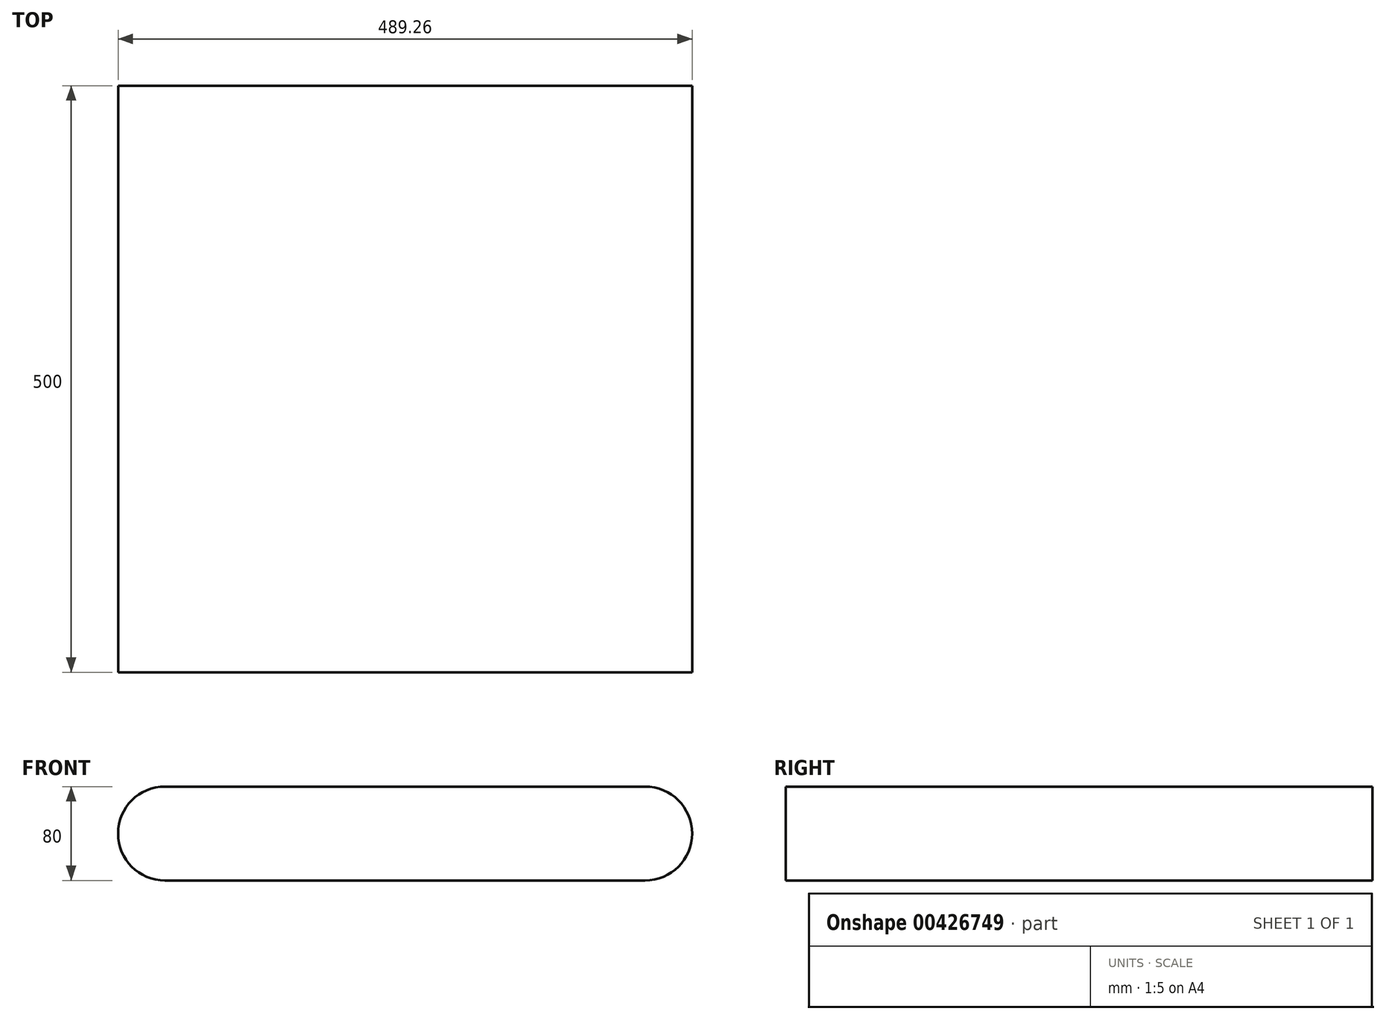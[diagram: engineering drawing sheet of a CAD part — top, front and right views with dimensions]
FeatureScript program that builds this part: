
annotation { "Feature Type Name" : "Feature", "Feature Type Description" : "" }
export const myFeature = defineFeature(function(context is Context, id is Id, definition is map)
    precondition{}
    {
        {
            var Q0;
            Q0=qCreatedBy(makeId("Front.planeOp"),FACE);
            var sketch = newSketch(context, id + "F0", { "sketchPlane" : qUnion([Q0])});
            skArc(sketch, "E0", {"start": v(0, -40) * mm, "mid": v(40, 0) * mm, "end": v(0, 40) * mm});
            skLineSegment(sketch, "E1", {"start": v(0, 40) * mm, "end": v(-409.26, 40) * mm});
            skLineSegment(sketch, "E2", {"start": v(0, -40) * mm, "end": v(-409.26, -40) * mm});
            skLineSegment(sketch, "E3", {"start": v(-449.25, -1.02) * mm, "end": v(-449.25, -1.02) * mm});
            skPoint(sketch, "E4.visualSharp", {"position": v(-450.3, 40) * mm});
            skArc(sketch, "E4.filletArc", {"start": v(-409.26, 40) * mm, "mid": v(-437.9, 27.92) * mm, "end": v(-449.25, -1.02) * mm});
            skPoint(sketch, "E5.visualSharp", {"position": v(-448.25, -40) * mm});
            skArc(sketch, "E5.filletArc", {"start": v(-449.25, -1.02) * mm, "mid": v(-437.18, -28.64) * mm, "end": v(-409.26, -40) * mm});
            skSolve(sketch);
        }
        {
            var Q0;
            Q0=makeQuery(id+"F0.imprint","IMPRINT",FACE,{"disambiguationData":[TD([[makeQuery(id+"F0.imprint","IMPRINT",EDGE,{"derivedFrom":sQuery(id+"F0.wireOp",EDGE,"E0")}),1.0]])]});
            extrude(context, id + "F1", {"entities" : qUnion([Q0]), "endBound" : BoundingType.SYMMETRIC, "depth" : 500 * mm});
        }
    });
